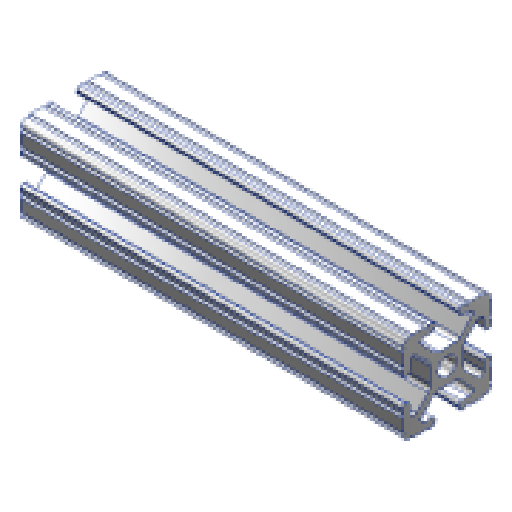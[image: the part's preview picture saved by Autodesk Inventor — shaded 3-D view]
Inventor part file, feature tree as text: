
AUTODESK INVENTOR PART (.ipt)
format: ipt  version: 2025 (Build 290162000, 162)  size: 226,816 bytes
history: native  units: in
note: dims shown in document units (in); Inventor stores cm internally (conversion verified against a paired STEP export)
features: extrude x1, sketch x1
ambient origin geometry x8: Origin, YZ Plane, XZ Plane, XY Plane, X Axis, Y Axis, Z Axis, Center Point
bodies: Solid1 (feature_tree)
feature tree (2):
  extrude  "Extrusion1"  [1 undecoded]
  sketch  "Sketch1"  dims[d0=4.25in d1=0.0in]
note: 1 required parameter value undecoded (feature->parameter linkage not recoverable at this tier; creation-order binding heuristic only, values carry confidence <= 0.55)
